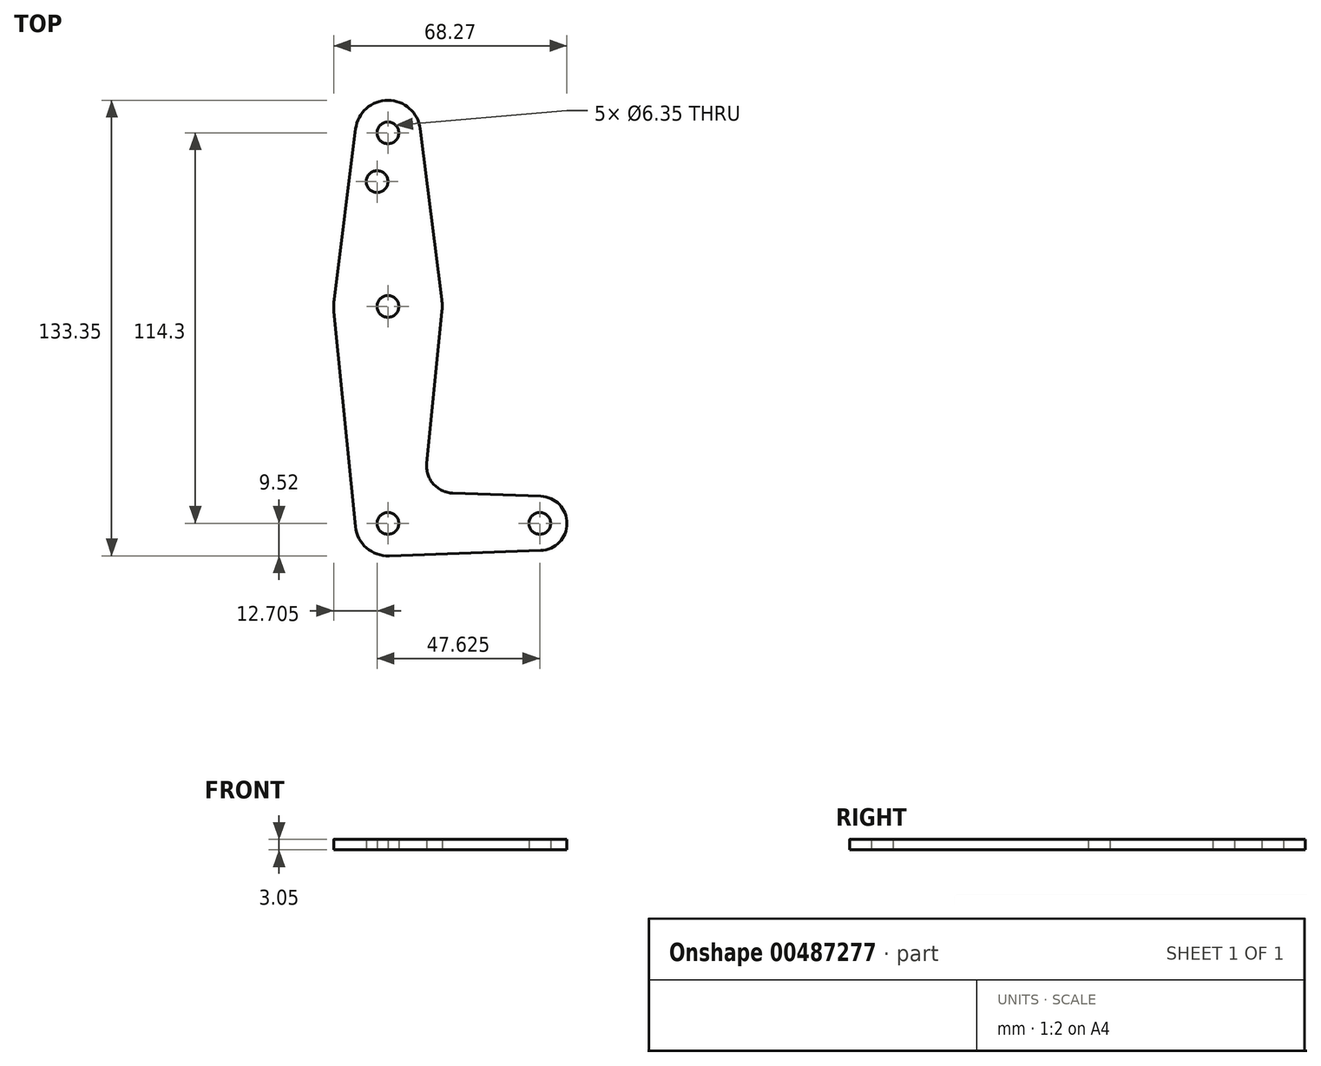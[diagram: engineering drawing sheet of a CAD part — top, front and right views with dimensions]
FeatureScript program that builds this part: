
annotation { "Feature Type Name" : "Feature", "Feature Type Description" : "" }
export const myFeature = defineFeature(function(context is Context, id is Id, definition is map)
    precondition{}
    {
        {
            var Q0;
            Q0=qCreatedBy(makeId("Top.planeOp"),FACE);
            var sketch = newSketch(context, id + "F0", { "sketchPlane" : qUnion([Q0])});
            skLineSegment(sketch, "E0", {"start": v(0, 0) * mm, "end": v(0, 114.3) * mm, "construction": true});
            skLineSegment(sketch, "E1", {"start": v(0, 0) * mm, "end": v(44.45, 0) * mm, "construction": true});
            skCircle(sketch, "E2", {"center": v(0, 114.3) * mm, "radius": 9.53 * mm});
            skCircle(sketch, "E3", {"center": v(0, 0) * mm, "radius": 9.53 * mm});
            skCircle(sketch, "E4", {"center": v(44.45, 0) * mm, "radius": 7.94 * mm});
            skCircle(sketch, "E5", {"center": v(0, 63.5) * mm, "radius": 15.88 * mm});
            skLineSegment(sketch, "E6", {"start": v(9.45, 115.5) * mm, "end": v(15.75, 65.48) * mm});
            skLineSegment(sketch, "E7", {"start": v(-9.45, 115.5) * mm, "end": v(-15.75, 65.48) * mm});
            skLineSegment(sketch, "E8", {"start": v(15.8, 61.91) * mm, "end": v(11.34, 17.6) * mm});
            skLineSegment(sketch, "E9", {"start": v(-9.48, -0.95) * mm, "end": v(-15.8, 61.91) * mm});
            skLineSegment(sketch, "E10", {"start": v(18.97, 8.85) * mm, "end": v(44.73, 7.93) * mm});
            skLineSegment(sketch, "E11", {"start": v(44.73, -7.93) * mm, "end": v(0.34, -9.52) * mm});
            skCircle(sketch, "E12", {"center": v(0, 114.3) * mm, "radius": 3.18 * mm});
            skCircle(sketch, "E13", {"center": v(0, 63.5) * mm, "radius": 3.17 * mm});
            skCircle(sketch, "E14", {"center": v(0, 0) * mm, "radius": 3.18 * mm});
            skCircle(sketch, "E15", {"center": v(44.45, 0) * mm, "radius": 3.18 * mm});
            skCircle(sketch, "E16", {"center": v(-3.18, 100.03) * mm, "radius": 3.18 * mm});
            skArc(sketch, "E17.filletArc", {"start": v(11.34, 17.6) * mm, "mid": v(13.26, 11.57) * mm, "end": v(18.97, 8.85) * mm});
            skSolve(sketch);
        }
        {
            var Q0;
            Q0 = qSketchRegion(id + "F0", true);
            extrude(context, id + "F1", {"entities" : qUnion([Q0]), "depth" : 3.05 * mm});
        }
    });
